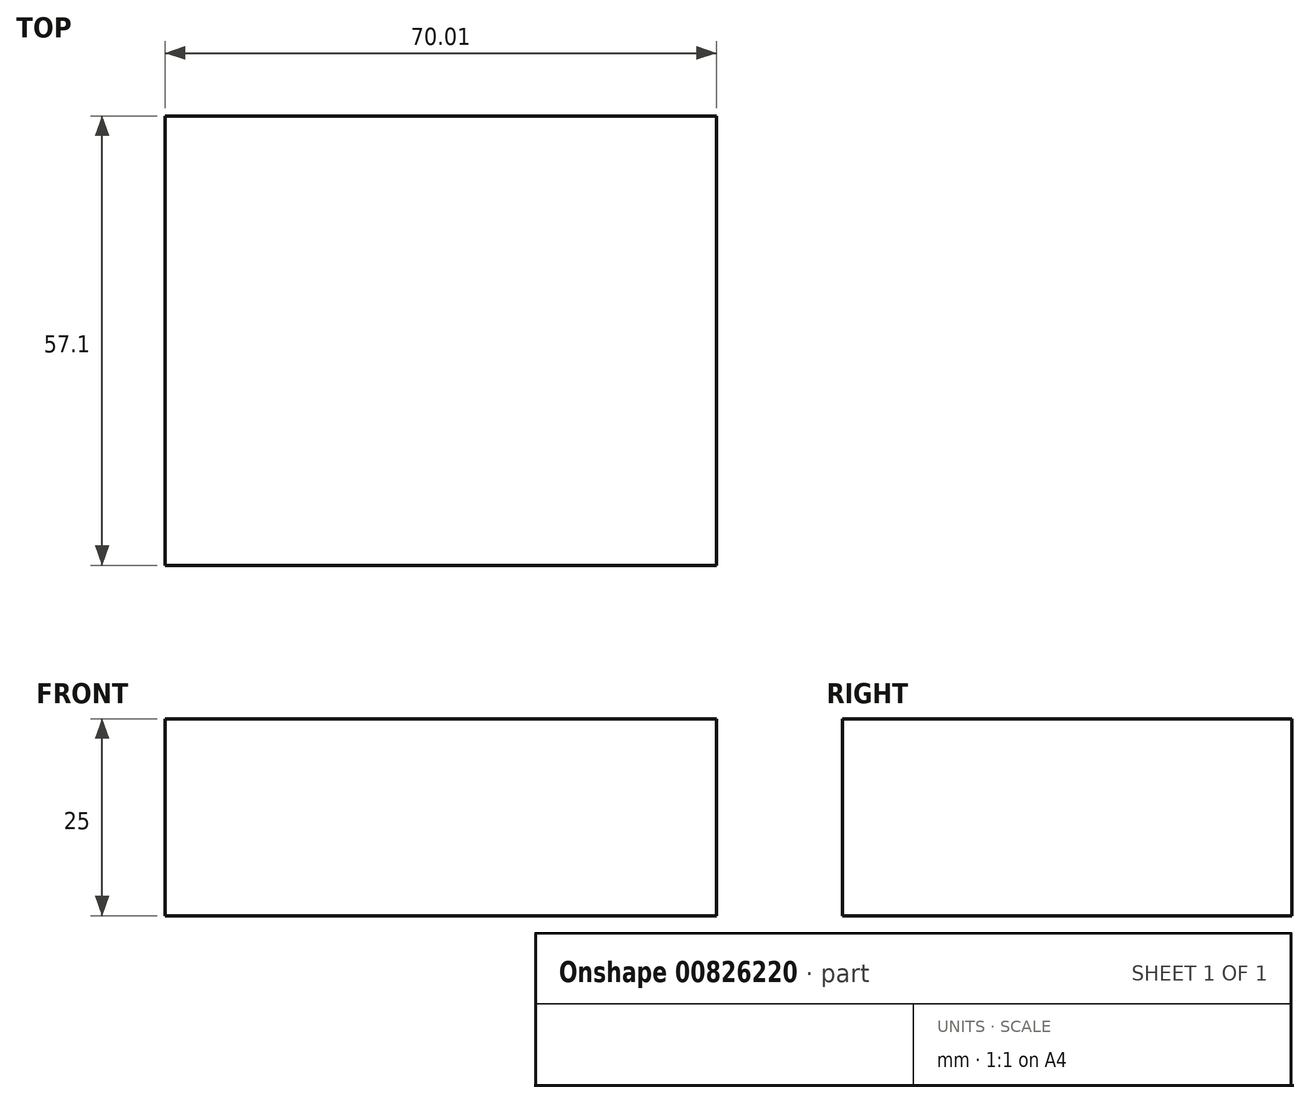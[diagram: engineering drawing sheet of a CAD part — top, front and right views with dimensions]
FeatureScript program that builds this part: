
annotation { "Feature Type Name" : "Feature", "Feature Type Description" : "" }
export const myFeature = defineFeature(function(context is Context, id is Id, definition is map)
    precondition{}
    {
        {
            var Q0;
            Q0=qCreatedBy(makeId("Top.planeOp"),FACE);
            var sketch = newSketch(context, id + "F0", { "sketchPlane" : qUnion([Q0])});
            skLineSegment(sketch, "E0.bottom", {"start": v(0, 0) * mm, "end": v(70, 0) * mm});
            skLineSegment(sketch, "E0.top", {"start": v(0, -57.1) * mm, "end": v(70, -57.1) * mm});
            skLineSegment(sketch, "E0.left", {"start": v(0, 0) * mm, "end": v(0, -57.1) * mm});
            skLineSegment(sketch, "E0.right", {"start": v(70, 0) * mm, "end": v(70, -57.1) * mm});
            skSolve(sketch);
        }
        {
            var Q0;
            Q0 = qSketchRegion(id + "F0", true);
            extrude(context, id + "F1", {"entities" : qUnion([Q0]), "depth" : 25 * mm, "offsetDistance" : 25 * mm});
        }
    });
